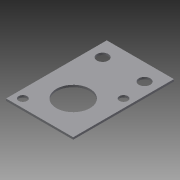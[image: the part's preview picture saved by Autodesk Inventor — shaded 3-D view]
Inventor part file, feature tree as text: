
AUTODESK INVENTOR PART (.ipt)
format: ipt  version: 2013 (Build 170138000, 138)  size: 99,840 bytes
history: native  units: in
note: dims shown in document units (in); Inventor stores cm internally (conversion verified against a paired STEP export)
features: extrude x1, sketch x1
ambient origin geometry x8: Origin, YZ Plane, XZ Plane, XY Plane, X Axis, Y Axis, Z Axis, Center Point
bodies: Solid1 (feature_tree)
feature tree (2):
  extrude  "Extrusion1"  Depth=1.0in
  sketch  "Sketch1"  dims[d0=0.5in d2=1.0in d3=1.0in d4=0.5in d5=0.125in d6=0.125in d7=0.1695in d8=0.1695in d9=0.125in d10=0.125in d11=0.125in d12=0.125in d13=0.5in d14=0.5in d15=0.25in d16=0.25in d17=0.625in d18=0.1875in d19=0.031in d20=0.0in]
